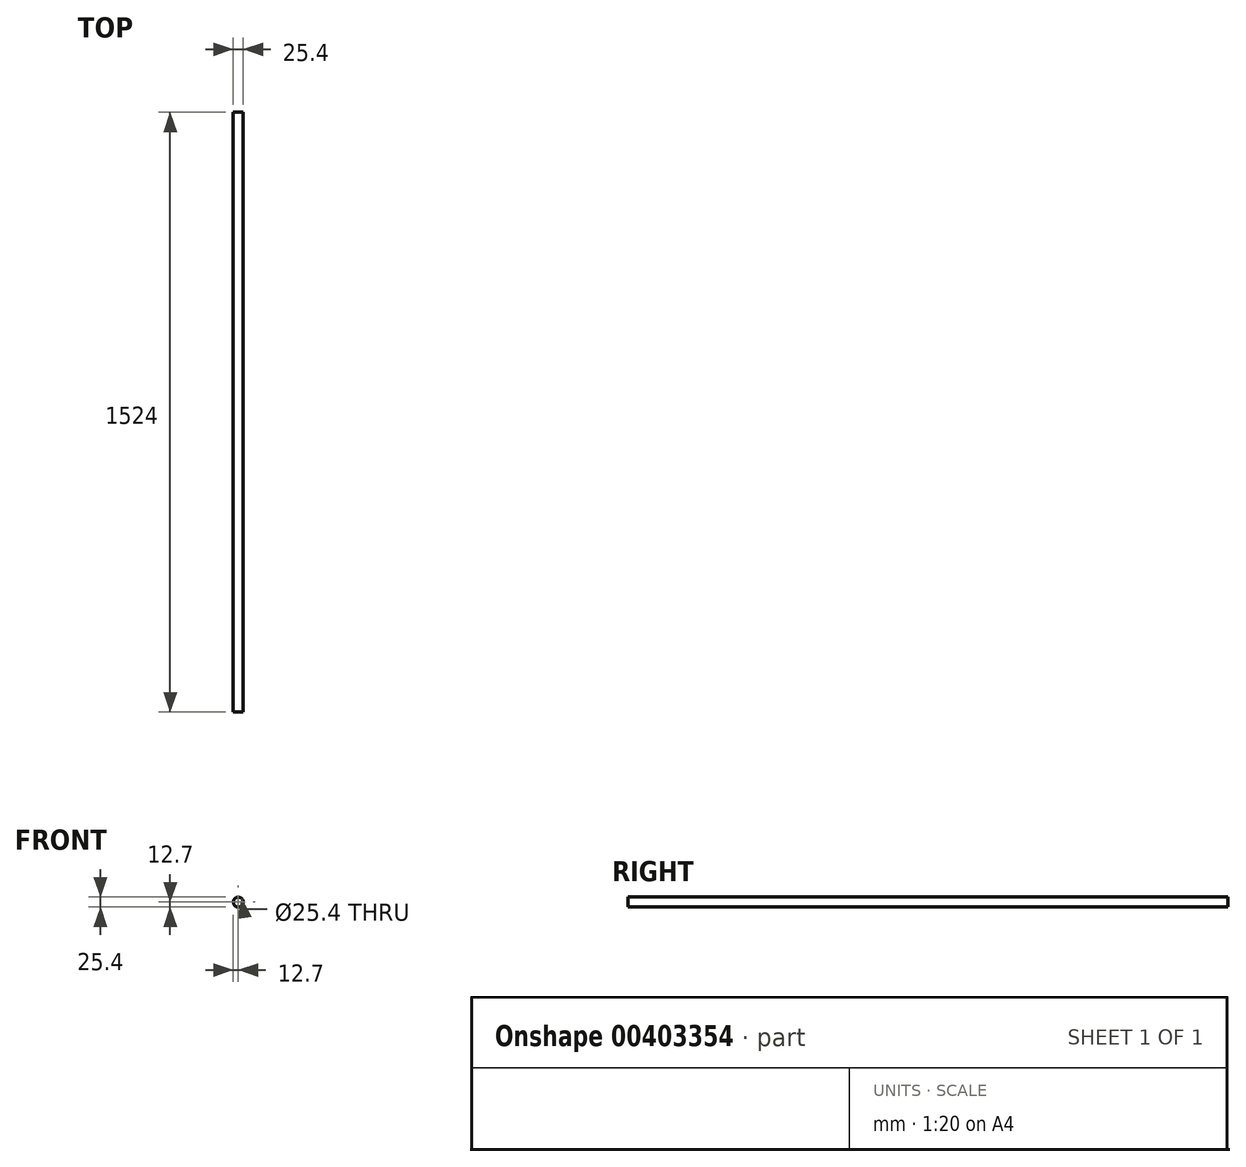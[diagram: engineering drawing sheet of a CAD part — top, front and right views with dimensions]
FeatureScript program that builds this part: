
annotation { "Feature Type Name" : "Feature", "Feature Type Description" : "" }
export const myFeature = defineFeature(function(context is Context, id is Id, definition is map)
    precondition{}
    {
        {
            var Q0;
            Q0=qCreatedBy(makeId("Front.planeOp"),FACE);
            var sketch = newSketch(context, id + "F0", { "sketchPlane" : qUnion([Q0])});
            skCircle(sketch, "E0", {"center": v(0, 0) * mm, "radius": 12.7 * mm});
            skSolve(sketch);
        }
        {
            var Q0;
            Q0=sQuery(id+"F0.wireOp",EDGE,"E0");
            var Q1;
            Q1=qCreatedBy(makeId("Front.planeOp"),FACE);
            extrude(context, id + "F1", {"bodyType" : ToolBodyType.SURFACE, "surfaceEntities" : qUnion([Q0]), "endBound" : BoundingType.SYMMETRIC, "oppositeDirection" : true, "endBoundEntityFace" : qUnion([Q1]), "depth" : 1524 * mm});
        }
    });
